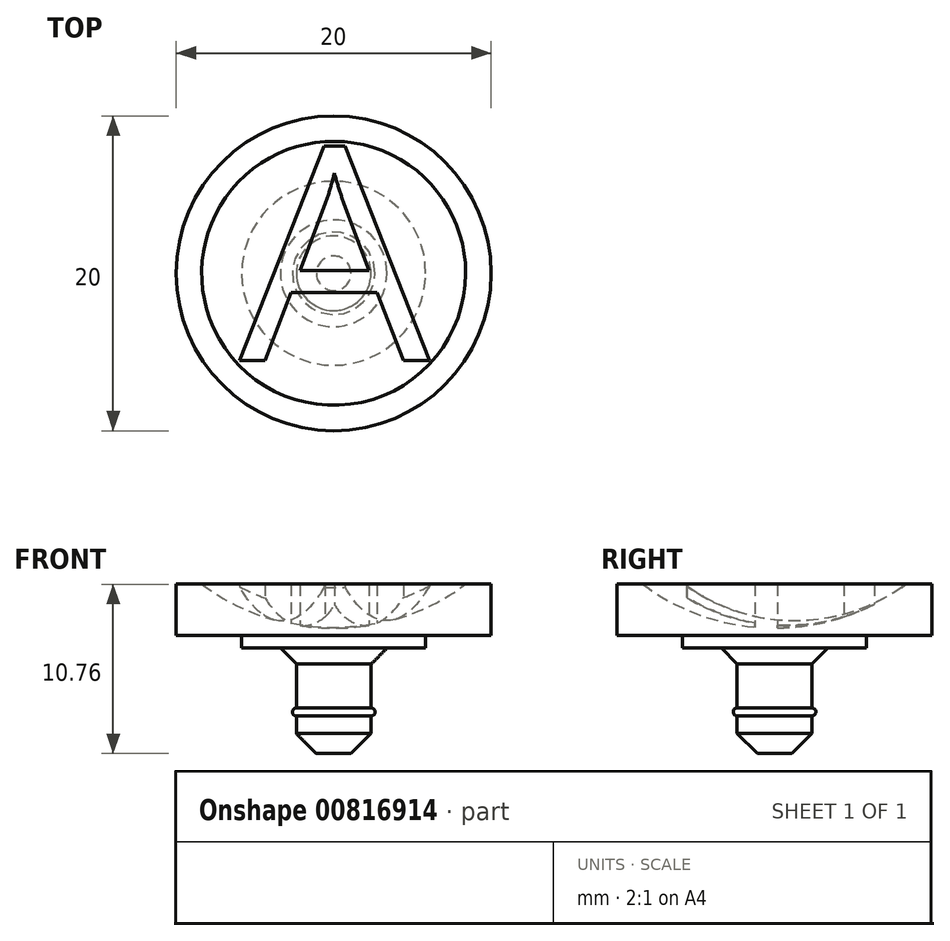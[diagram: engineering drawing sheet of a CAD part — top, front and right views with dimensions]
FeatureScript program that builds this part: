
annotation { "Feature Type Name" : "Feature", "Feature Type Description" : "" }
export const myFeature = defineFeature(function(context is Context, id is Id, definition is map)
    precondition{}
    {
        {
            var Q0;
            Q0=qCreatedBy(makeId("Front.planeOp"),FACE);
            var sketch = newSketch(context, id + "F0", { "sketchPlane" : qUnion([Q0])});
            skLineSegment(sketch, "E0", {"start": v(4.22, 0) * mm, "end": v(10, 0) * mm});
            skLineSegment(sketch, "E1", {"start": v(10, 0) * mm, "end": v(10, 5.48) * mm});
            skArc(sketch, "E2", {"start": v(0, 1.27) * mm, "mid": v(5.43, 2.37) * mm, "end": v(10, 5.48) * mm});
            skLineSegment(sketch, "E3", {"start": v(0, 1.27) * mm, "end": v(0, 0) * mm});
            skLineSegment(sketch, "E4", {"start": v(2.37, 0) * mm, "end": v(2.68, 0) * mm});
            skLineSegment(sketch, "E5", {"start": v(2.37, 0) * mm, "end": v(2.37, -3.8) * mm});
            skLineSegment(sketch, "E6", {"start": v(2.37, -6.7) * mm, "end": v(0, -6.7) * mm});
            skLineSegment(sketch, "E7", {"start": v(0, -6.7) * mm, "end": v(0, 0) * mm});
            skArc(sketch, "E8", {"start": v(2.37, -4.3) * mm, "mid": v(2.63, -4.05) * mm, "end": v(2.37, -3.8) * mm});
            skLineSegment(sketch, "E9.trimOffspring", {"start": v(2.37, -4.3) * mm, "end": v(2.37, -6.7) * mm});
            skLineSegment(sketch, "E10", {"start": v(2.68, 0) * mm, "end": v(4.22, 0) * mm});
            skSolve(sketch);
        }
        {
            var Q0;
            Q0=qSketchRegion(id+"F0",true);
            var Q1;
            Q1=sQuery(id+"F0.wireOp",EDGE,"E3");
            revolve(context, id + "F1", {"surfaceOperationType" : NewSurfaceOperationType.NEW, "entities" : qUnion([Q0]), "axis" : qUnion([Q1]), "revolveType" : RevolveType.FULL});
        }
        {
            var Q0;
            Q0=qCreatedBy(makeId("Top.planeOp"),FACE);
            var sketch = newSketch(context, id + "F2", { "sketchPlane" : qUnion([Q0])});
            skText(sketch, "E11", { "text": "A", "fontName": "OpenSans-Regular.ttf"});
            const initialGuessF2  = {"E11": [-0.00597, -0.00555, 1, 0, 0.0137]};
            skSetInitialGuess(sketch, initialGuessF2);
            skSolve(sketch);
        }
        {
            var Q0;
            Q0 = qSketchRegion(id + "F2", true);
            extrude(context, id + "F3", {"entities" : qUnion([Q0]), "operationType" : NewBodyOperationType.ADD, "depth" : 4.06 * mm, "offsetDistance" : 25.4 * mm});
        }
        {
            var Q0;
            Q0=qCreatedBy(makeId("Right.planeOp"),FACE);
            var sketch = newSketch(context, id + "F4", { "sketchPlane" : qUnion([Q0])});
            skLineSegment(sketch, "E12.bottom", {"start": v(-221.51, 121.4) * mm, "end": v(217.82, 121.4) * mm});
            skLineSegment(sketch, "E12.top", {"start": v(-221.51, 4.06) * mm, "end": v(217.82, 4.06) * mm});
            skLineSegment(sketch, "E12.left", {"start": v(-221.51, 121.4) * mm, "end": v(-221.51, 4.06) * mm});
            skLineSegment(sketch, "E12.right", {"start": v(217.82, 121.4) * mm, "end": v(217.82, 4.06) * mm});
            skSolve(sketch);
        }
        {
            var Q0;
            Q0 = qSketchRegion(id + "F4", true);
            extrude(context, id + "F5", {"entities" : qUnion([Q0]), "operationType" : NewBodyOperationType.REMOVE, "endBound" : BoundingType.SYMMETRIC, "depth" : 25.4 * mm, "offsetDistance" : 25.4 * mm});
        }
        {
            var Q0;
            Q0=makeQuery(id+"F1.opRevolve","SWEPT_EDGE",EDGE,{"disambiguationData":[OSD([sQuery(id+"F0.wireOp",EDGE,"E6"),sQuery(id+"F0.wireOp",EDGE,"E9.trimOffspring")])]});
            chamfer(context, id + "F6", {"entities" : qUnion([Q0]), "width" : 1.27 * mm, "tangentPropagation" : true});
        }
        {
            var Q0;
            Q0=makeQuery(id+"F1.opRevolve","SWEPT_FACE",FACE,{"disambiguationData":[OSD([sQuery(id+"F0.wireOp",EDGE,"E0"),sQuery(id+"F0.wireOp",EDGE,"E4"),sQuery(id+"F0.wireOp",EDGE,"E10")])]});
            var sketch = newSketch(context, id + "F7", { "sketchPlane" : qUnion([Q0])});
            skCircle(sketch, "E13", {"center": v(0, 0) * mm, "radius": 5.84 * mm});
            skCircle(sketch, "E14", {"center": v(0, 0) * mm, "radius": 18.58 * mm});
            skSolve(sketch);
        }
        {
            var Q0;
            Q0 = qSketchRegion(id + "F7", true);
            extrude(context, id + "F8", {"entities" : qUnion([Q0]), "operationType" : NewBodyOperationType.REMOVE, "oppositeDirection" : true, "depth" : .8 * mm, "offsetDistance" : 25.4 * mm});
        }
        {
            var Q0;
            Q0=makeQuery(id+"F1.opRevolve","SWEPT_EDGE",EDGE,{"disambiguationData":[OSD([sQuery(id+"F0.wireOp",EDGE,"E4"),sQuery(id+"F0.wireOp",EDGE,"E5")])]});
            chamfer(context, id + "F9", {"entities" : qUnion([Q0]), "width" : 1.02 * mm, "tangentPropagation" : true});
        }
    });
